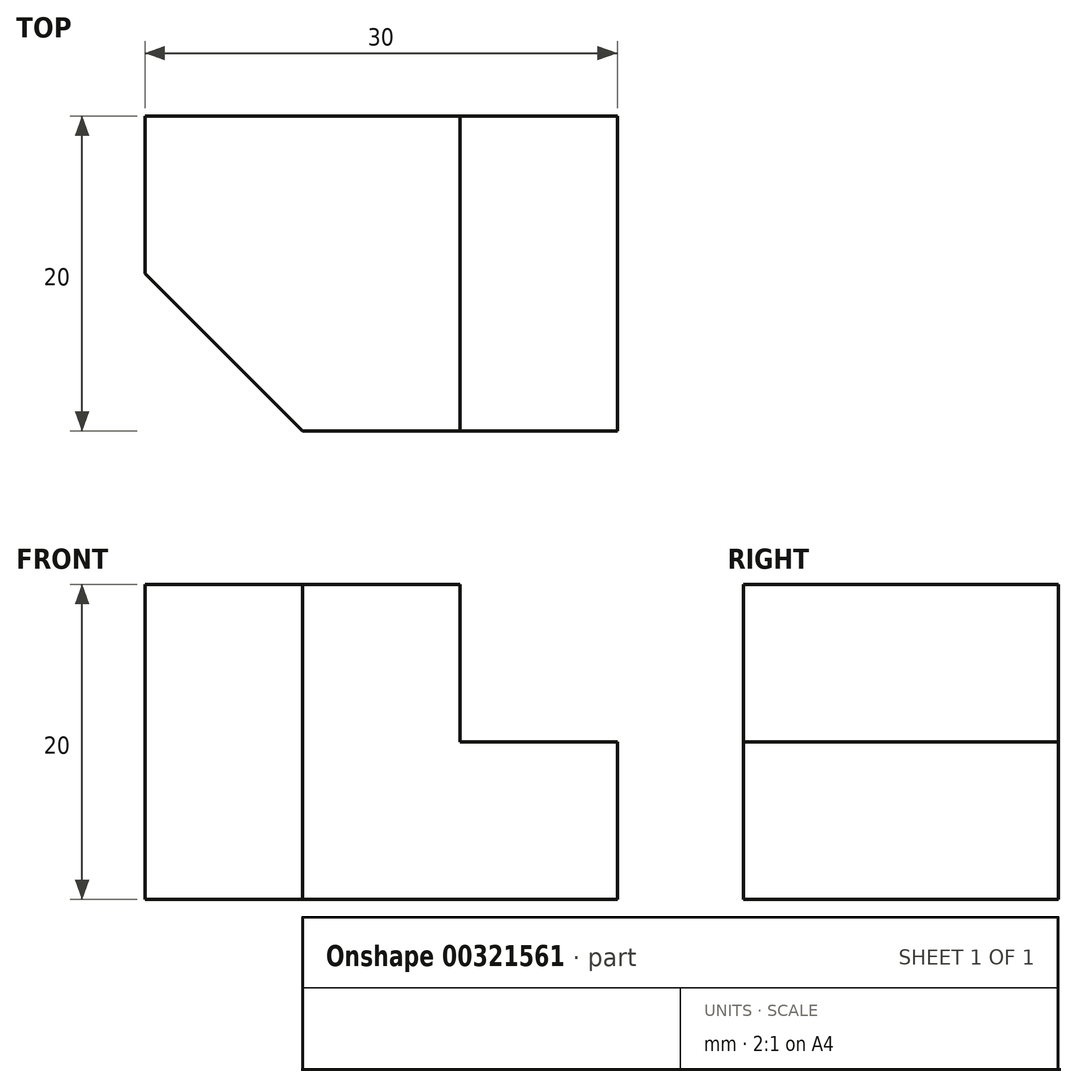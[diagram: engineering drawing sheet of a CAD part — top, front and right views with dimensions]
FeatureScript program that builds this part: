
annotation { "Feature Type Name" : "Feature", "Feature Type Description" : "" }
export const myFeature = defineFeature(function(context is Context, id is Id, definition is map)
    precondition{}
    {
        {
            var Q0;
            Q0=qCreatedBy(makeId("Top.planeOp"),FACE);
            var sketch = newSketch(context, id + "F0", { "sketchPlane" : qUnion([Q0])});
            skLineSegment(sketch, "E0", {"start": v(0, 0) * mm, "end": v(-10, 10) * mm});
            skLineSegment(sketch, "E1", {"start": v(-10, 10) * mm, "end": v(-10, 20) * mm});
            skLineSegment(sketch, "E2", {"start": v(-10, 20) * mm, "end": v(20, 20) * mm});
            skLineSegment(sketch, "E3", {"start": v(20, 20) * mm, "end": v(20, 0) * mm});
            skLineSegment(sketch, "E4", {"start": v(20, 0) * mm, "end": v(0, 0) * mm});
            skSolve(sketch);
        }
        {
            var Q0;
            Q0 = qSketchRegion(id + "F0", true);
            extrude(context, id + "F1", {"entities" : qUnion([Q0]), "depth" : 20 * mm});
        }
        {
            var Q0;
            Q0=qCreatedBy(makeId("Front.planeOp"),FACE);
            var sketch = newSketch(context, id + "F2", { "sketchPlane" : qUnion([Q0])});
            skLineSegment(sketch, "E5.0", {"start": v(20, 20) * mm, "end": v(10, 20) * mm});
            skLineSegment(sketch, "E6.0", {"start": v(20, 20) * mm, "end": v(20, 10) * mm});
            skLineSegment(sketch, "E7.top", {"start": v(20, 10) * mm, "end": v(10, 10) * mm});
            skLineSegment(sketch, "E7.right", {"start": v(10, 20) * mm, "end": v(10, 10) * mm});
            skPoint(sketch, "E8.orphan", {"position": v(0, 20) * mm});
            skPoint(sketch, "E9.orphan", {"position": v(20, 0) * mm});
            skSolve(sketch);
        }
        {
            var Q0;
            Q0 = qSketchRegion(id + "F2", true);
            extrude(context, id + "F3", {"entities" : qUnion([Q0]), "operationType" : NewBodyOperationType.REMOVE, "endBound" : BoundingType.THROUGH_ALL, "oppositeDirection" : true, "depth" : 25 * mm});
        }
    });
